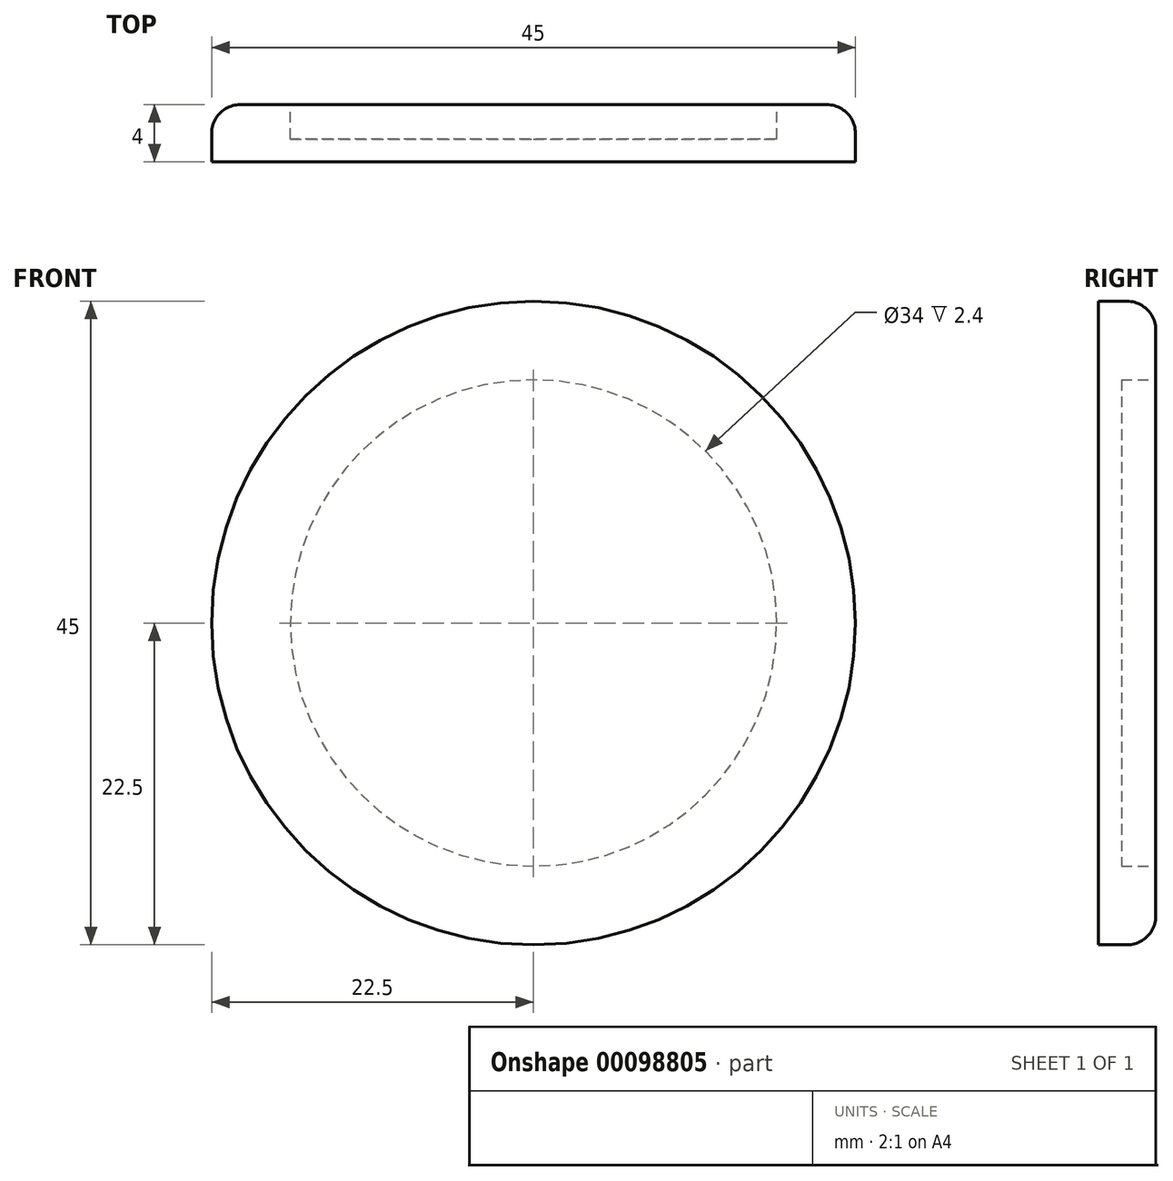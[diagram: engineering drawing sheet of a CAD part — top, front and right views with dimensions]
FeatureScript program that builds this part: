
annotation { "Feature Type Name" : "Feature", "Feature Type Description" : "" }
export const myFeature = defineFeature(function(context is Context, id is Id, definition is map)
    precondition{}
    {
        {
            var Q0;
            Q0=qCreatedBy(makeId("Top.planeOp"),FACE);
            var sketch = newSketch(context, id + "F0", { "sketchPlane" : qUnion([Q0])});
            skLineSegment(sketch, "E0", {"start": v(0, 5.2) * mm, "end": v(0, -5.04) * mm, "construction": true});
            skLineSegment(sketch, "E1", {"start": v(0, 1.6) * mm, "end": v(17, 1.6) * mm});
            skLineSegment(sketch, "E2", {"start": v(17, 1.6) * mm, "end": v(17, 4) * mm});
            skLineSegment(sketch, "E3", {"start": v(17, 4) * mm, "end": v(22.5, 4) * mm});
            skLineSegment(sketch, "E4", {"start": v(22.5, 4) * mm, "end": v(22.5, 0) * mm});
            skLineSegment(sketch, "E5", {"start": v(22.5, 0) * mm, "end": v(0, 0) * mm});
            skLineSegment(sketch, "E6", {"start": v(0, 0) * mm, "end": v(0, 1.6) * mm});
            skSolve(sketch);
        }
        {
            var Q0;
            Q0 = qSketchRegion(id + "F0", true);
            var Q1;
            Q1=sQuery(id+"F0.wireOp",EDGE,"E0");
            revolve(context, id + "F1", {"entities" : qUnion([Q0]), "axis" : qUnion([Q1]), "revolveType" : RevolveType.FULL});
        }
        {
            var Q0;
            Q0=makeQuery(id+"F1.opRevolve","SWEPT_EDGE",EDGE,{"disambiguationData":[OSD([sQuery(id+"F0.wireOp",EDGE,"E3"),sQuery(id+"F0.wireOp",EDGE,"E4")])]});
            fillet(context, id + "F2", {"entities" : qUnion([Q0]), "radius" : 2 * mm, "tangentPropagation" : true, "allowEdgeOverflow" : false});
        }
    });
